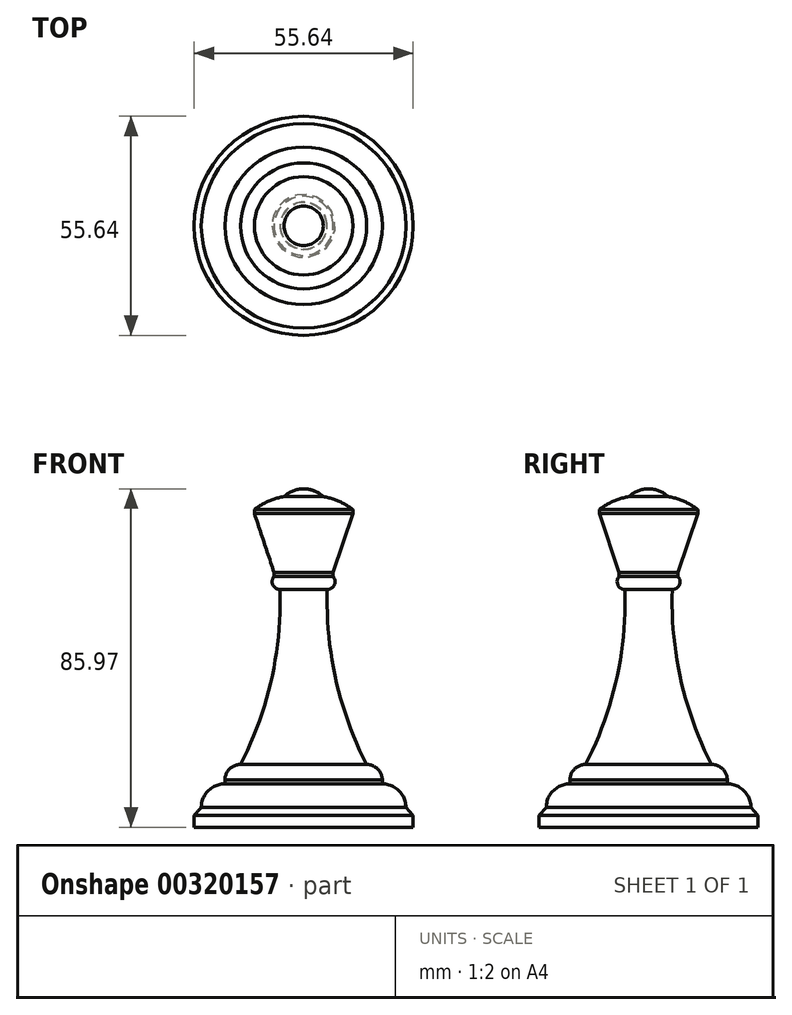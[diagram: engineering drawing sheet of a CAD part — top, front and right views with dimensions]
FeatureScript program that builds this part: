
annotation { "Feature Type Name" : "Feature", "Feature Type Description" : "" }
export const myFeature = defineFeature(function(context is Context, id is Id, definition is map)
    precondition{}
    {
        {
            var Q0;
            Q0=qCreatedBy(makeId("Front.planeOp"),FACE);
            var sketch = newSketch(context, id + "F0", { "sketchPlane" : qUnion([Q0])});
            skArc(sketch, "E0", {"start": v(0, 0) * mm, "mid": v(2.7, -0.52) * mm, "end": v(5, -2) * mm});
            skLineSegment(sketch, "E1", {"start": v(12.5, -5.27) * mm, "end": v(0, -5.27) * mm});
            skArc(sketch, "E2", {"start": v(12.5, -5.27) * mm, "mid": v(6.6, -2.33) * mm, "end": v(0, -2) * mm});
            skLineSegment(sketch, "E3", {"start": v(12.5, -6.27) * mm, "end": v(0, -6.27) * mm});
            skLineSegment(sketch, "E4", {"start": v(12.5, -6.27) * mm, "end": v(12.5, -5.27) * mm});
            skLineSegment(sketch, "E5", {"start": v(7.5, -21.27) * mm, "end": v(0, -21.27) * mm});
            skLineSegment(sketch, "E6", {"start": v(7.5, -22.27) * mm, "end": v(0, -22.27) * mm});
            skLineSegment(sketch, "E7", {"start": v(7.5, -22.27) * mm, "end": v(7.5, -21.27) * mm});
            skLineSegment(sketch, "E8", {"start": v(12.5, -6.27) * mm, "end": v(7.5, -21.27) * mm});
            skArc(sketch, "E9", {"start": v(6, -25.59) * mm, "mid": v(7.82, -24.41) * mm, "end": v(7.5, -22.27) * mm});
            skLineSegment(sketch, "E10", {"start": v(6, -25.6) * mm, "end": v(0, -25.6) * mm});
            skArc(sketch, "E11", {"start": v(6, -25.6) * mm, "mid": v(8.17, -48.44) * mm, "end": v(16, -70.02) * mm});
            skArc(sketch, "E12", {"start": v(20, -73.97) * mm, "mid": v(18.81, -71.17) * mm, "end": v(16, -70.02) * mm});
            skLineSegment(sketch, "E13", {"start": v(20, -73.97) * mm, "end": v(0, -73.97) * mm});
            skLineSegment(sketch, "E14", {"start": v(20, -74.97) * mm, "end": v(0, -74.97) * mm});
            skLineSegment(sketch, "E15", {"start": v(20, -74.97) * mm, "end": v(20, -73.97) * mm});
            skArc(sketch, "E16", {"start": v(26, -80.97) * mm, "mid": v(24.24, -76.73) * mm, "end": v(20, -74.97) * mm});
            skLineSegment(sketch, "E17", {"start": v(26, -80.97) * mm, "end": v(27.82, -82.97) * mm});
            skLineSegment(sketch, "E18", {"start": v(27.82, -82.97) * mm, "end": v(0, -82.97) * mm});
            skLineSegment(sketch, "E19", {"start": v(26, -80.97) * mm, "end": v(0, -80.97) * mm});
            skLineSegment(sketch, "E20", {"start": v(27.82, -82.97) * mm, "end": v(27.82, -85.97) * mm});
            skLineSegment(sketch, "E21", {"start": v(27.82, -85.97) * mm, "end": v(0, -85.97) * mm});
            skLineSegment(sketch, "E22", {"start": v(0, -85.97) * mm, "end": v(0, 0) * mm});
            skSolve(sketch);
        }
        {
            var Q0;
            Q0 = qSketchRegion(id + "F0", true);
            var Q1;
            Q1=sQuery(id+"F0.wireOp",EDGE,"E22");
            revolve(context, id + "F1", {"entities" : qUnion([Q0]), "axis" : qUnion([Q1]), "revolveType" : RevolveType.FULL});
        }
    });
